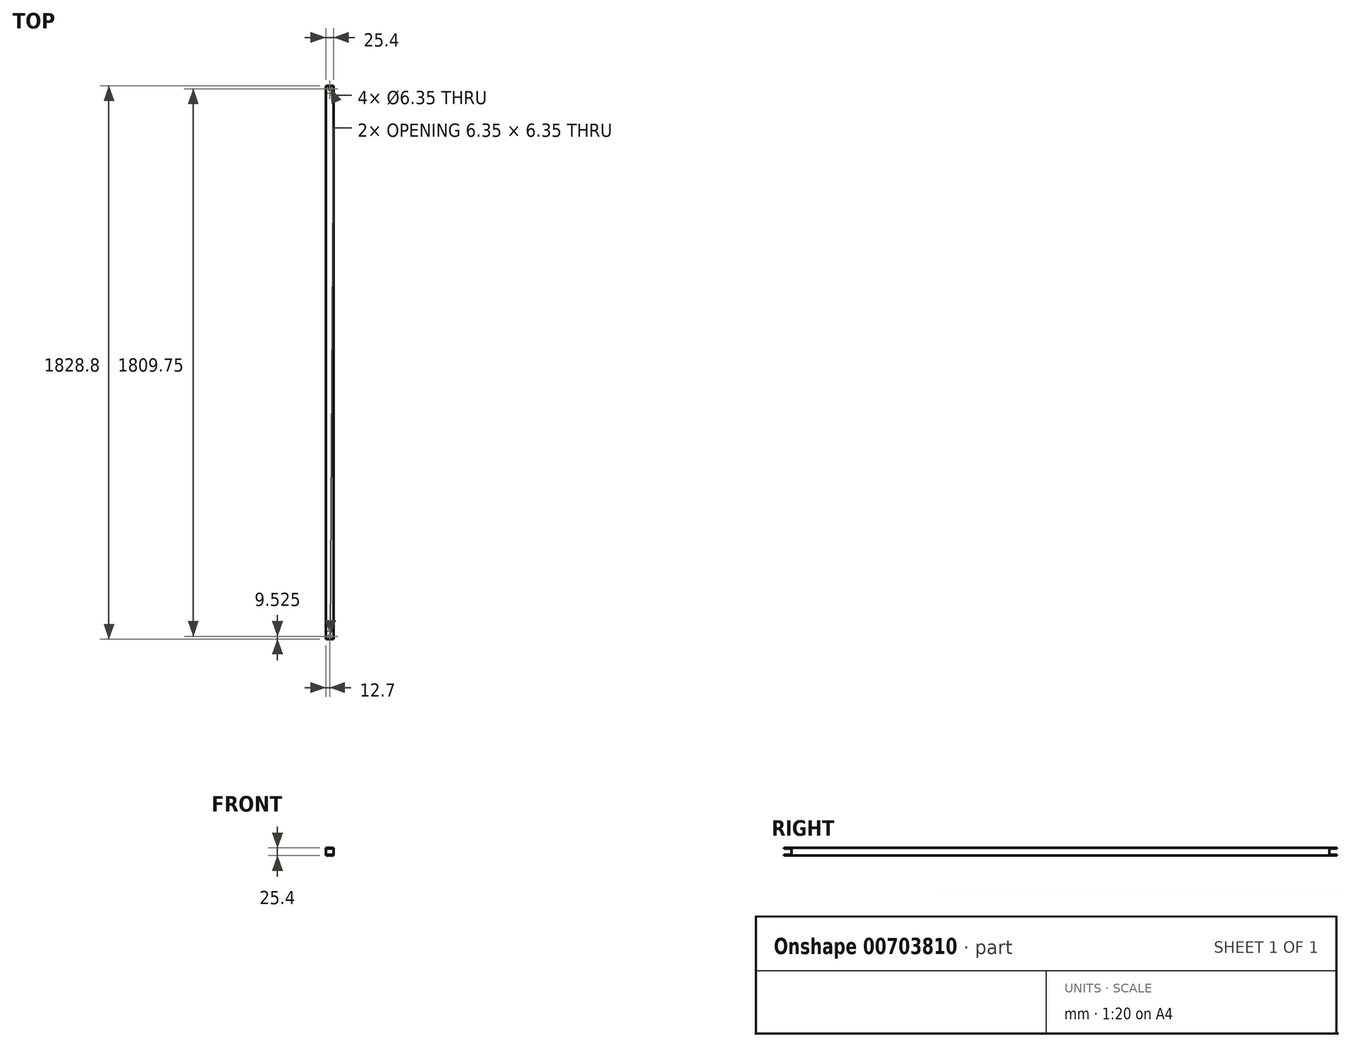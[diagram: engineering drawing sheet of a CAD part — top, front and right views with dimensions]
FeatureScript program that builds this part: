
annotation { "Feature Type Name" : "Feature", "Feature Type Description" : "" }
export const myFeature = defineFeature(function(context is Context, id is Id, definition is map)
    precondition{}
    {
        {
            var Q0;
            Q0=qCreatedBy(makeId("Top.planeOp"),FACE);
            var sketch = newSketch(context, id + "F0", { "sketchPlane" : qUnion([Q0])});
            skLineSegment(sketch, "E0.bottom", {"start": v(-12.7, -914.4) * mm, "end": v(12.7, -914.4) * mm});
            skLineSegment(sketch, "E0.top", {"start": v(-12.7, 914.4) * mm, "end": v(12.7, 914.4) * mm});
            skLineSegment(sketch, "E0.left", {"start": v(-12.7, -914.4) * mm, "end": v(-12.7, 914.4) * mm});
            skLineSegment(sketch, "E0.right", {"start": v(12.7, -914.4) * mm, "end": v(12.7, 914.4) * mm});
            skPoint(sketch, "E0.middle", {"position": v(0, 0) * mm});
            skSolve(sketch);
        }
        {
            var Q0;
            Q0=makeQuery(id+"F0.imprint","IMPRINT",FACE,{"disambiguationData":[TD([[makeQuery(id+"F0.imprint","IMPRINT",EDGE,{"derivedFrom":sQuery(id+"F0.wireOp",EDGE,"E0.bottom")}),1.0]])]});
            extrude(context, id + "F1", {"entities" : qUnion([Q0]), "depth" : 25.4 * mm, "offsetDistance" : 25.4 * mm});
        }
        {
            var Q0;
            Q0=makeQuery(id+"F1.opExtrude","SWEPT_FACE",FACE,{"disambiguationData":[OSD([sQuery(id+"F0.wireOp",EDGE,"E0.left")])]});
            var sketch = newSketch(context, id + "F2", { "sketchPlane" : qUnion([Q0])});
            skLineSegment(sketch, "E1.bottom", {"start": v(-939.8, 2.54) * mm, "end": v(-889, 2.54) * mm});
            skLineSegment(sketch, "E1.top", {"start": v(-939.8, 22.86) * mm, "end": v(-889, 22.86) * mm});
            skLineSegment(sketch, "E1.left", {"start": v(-939.8, 2.54) * mm, "end": v(-939.8, 22.86) * mm});
            skLineSegment(sketch, "E1.right", {"start": v(-889, 2.54) * mm, "end": v(-889, 22.86) * mm});
            skPoint(sketch, "E1.middle", {"position": v(-914.4, 12.7) * mm});
            skSolve(sketch);
        }
        {
            var Q0;
            {var subQ0=sQuery(id+"F2.wireOp",EDGE,"E1.left");Q0=makeQuery(id+"F2.imprint","IMPRINT",FACE,{"disambiguationData":[TD([[makeQuery(id+"F2.imprint","IMPRINT",EDGE,{"derivedFrom":subQ0}),-1.0]])]});}
            var Q1;
            {var subQ0=sQuery(id+"F2.wireOp",EDGE,"E1.right");Q1=makeQuery(id+"F2.imprint","IMPRINT",FACE,{"disambiguationData":[TD([[makeQuery(id+"F2.imprint","IMPRINT",EDGE,{"derivedFrom":subQ0}),1.0]])]});}
            extrude(context, id + "F3", {"entities" : qUnion([Q0, Q1]), "operationType" : NewBodyOperationType.REMOVE, "oppositeDirection" : true, "depth" : 25.4 * mm, "offsetDistance" : 25.4 * mm});
        }
        {
            var Q0;
            Q0=makeQuery(id+"F1.opExtrude","SWEPT_FACE",FACE,{"disambiguationData":[OSD([sQuery(id+"F0.wireOp",EDGE,"E0.left")])]});
            var sketch = newSketch(context, id + "F4", { "sketchPlane" : qUnion([Q0])});
            skLineSegment(sketch, "E2.bottom", {"start": v(889, 2.54) * mm, "end": v(939.8, 2.54) * mm});
            skLineSegment(sketch, "E2.top", {"start": v(889, 22.86) * mm, "end": v(939.8, 22.86) * mm});
            skLineSegment(sketch, "E2.left", {"start": v(889, 2.54) * mm, "end": v(889, 22.86) * mm});
            skLineSegment(sketch, "E2.right", {"start": v(939.8, 2.54) * mm, "end": v(939.8, 22.86) * mm});
            skPoint(sketch, "E2.middle", {"position": v(914.4, 12.7) * mm});
            skSolve(sketch);
        }
        {
            var Q0;
            Q0 = qSketchRegion(id + "F4", true);
            extrude(context, id + "F5", {"entities" : qUnion([Q0]), "operationType" : NewBodyOperationType.REMOVE, "oppositeDirection" : true, "depth" : 25.4 * mm, "offsetDistance" : 25.4 * mm});
        }
        {
            var Q0;
            Q0=makeQuery(id+"F1.opExtrude","CAP_FACE",FACE,{"disambiguationData":[OSD([sQuery(id+"F0.wireOp",EDGE,"E0.bottom"),sQuery(id+"F0.wireOp",EDGE,"E0.top"),sQuery(id+"F0.wireOp",EDGE,"E0.left"),sQuery(id+"F0.wireOp",EDGE,"E0.right")])],"isStart":false});
            var sketch = newSketch(context, id + "F6", { "sketchPlane" : qUnion([Q0])});
            skCircle(sketch, "E3", {"center": v(0, -904.88) * mm, "radius": 3.18 * mm});
            skCircle(sketch, "E4", {"center": v(0, 904.88) * mm, "radius": 3.18 * mm});
            skSolve(sketch);
        }
        {
            var Q0;
            Q0=makeQuery(id+"F6.imprint","IMPRINT",FACE,{"disambiguationData":[TD([[makeQuery(id+"F6.imprint","IMPRINT",EDGE,{"derivedFrom":sQuery(id+"F6.wireOp",EDGE,"E4")}),1.0]])]});
            var Q1;
            Q1=makeQuery(id+"F6.imprint","IMPRINT",FACE,{"disambiguationData":[TD([[makeQuery(id+"F6.imprint","IMPRINT",EDGE,{"derivedFrom":sQuery(id+"F6.wireOp",EDGE,"E3")}),1.0]])]});
            extrude(context, id + "F7", {"entities" : qUnion([Q0, Q1]), "operationType" : NewBodyOperationType.REMOVE, "oppositeDirection" : true, "depth" : 50.8 * mm, "offsetDistance" : 25.4 * mm});
        }
    });
